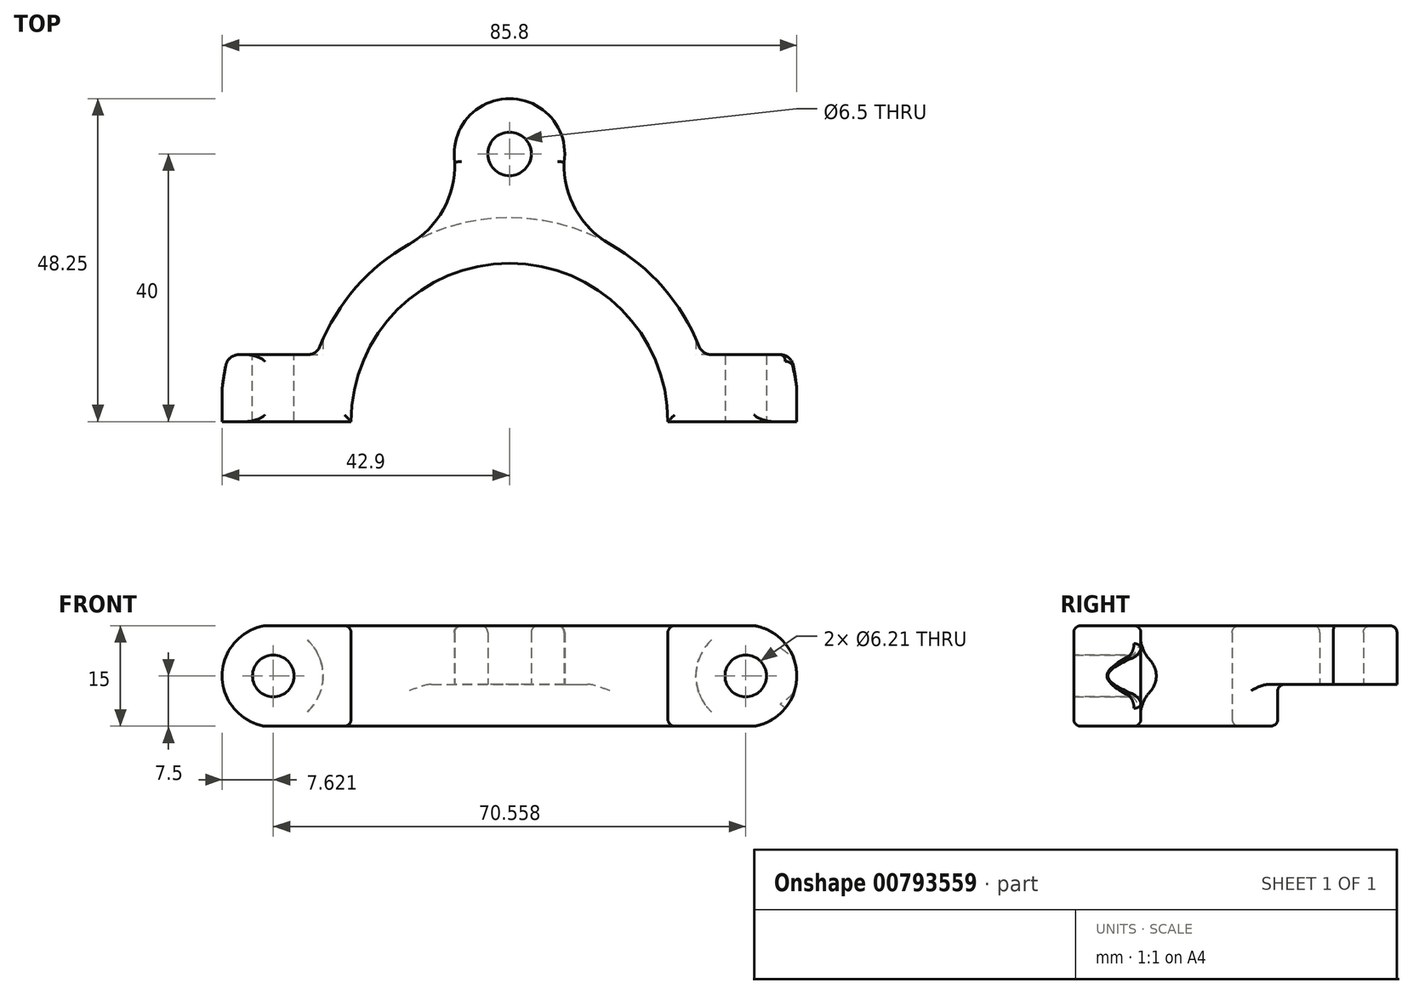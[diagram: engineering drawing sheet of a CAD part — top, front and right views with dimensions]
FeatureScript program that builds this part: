
annotation { "Feature Type Name" : "Feature", "Feature Type Description" : "" }
export const myFeature = defineFeature(function(context is Context, id is Id, definition is map)
    precondition{}
    {
        {
            var Q0;
            Q0=qCreatedBy(makeId("Top.planeOp"),FACE);
            var sketch = newSketch(context, id + "F0", { "sketchPlane" : qUnion([Q0])});
            skArc(sketch, "E0", {"start": v(23.65, 0) * mm, "mid": v(0, 23.65) * mm, "end": v(-23.65, 0) * mm});
            skLineSegment(sketch, "E1", {"start": v(-43.2, 0) * mm, "end": v(-23.65, 0) * mm});
            skLineSegment(sketch, "E2.0", {"start": v(-40.4, 10) * mm, "end": v(-30.15, 10) * mm});
            skArc(sketch, "E3", {"start": v(-42.37, 8.39) * mm, "mid": v(-42.99, 4.21) * mm, "end": v(-43.2, 0) * mm});
            skPoint(sketch, "E4.orphan", {"position": v(-60.74, 0) * mm});
            skArc(sketch, "E5.trimOffspring", {"start": v(43.2, 0) * mm, "mid": v(42.99, 4.21) * mm, "end": v(42.37, 8.39) * mm});
            skLineSegment(sketch, "E6.trimOffspring", {"start": v(30.15, 10) * mm, "end": v(40.4, 10) * mm});
            skLineSegment(sketch, "E7.trimOffspring", {"start": v(23.65, 0) * mm, "end": v(43.2, 0) * mm});
            skArc(sketch, "E8.trimOffspring", {"start": v(28.3, 11.26) * mm, "mid": v(27.77, 12.48) * mm, "end": v(27.2, 13.68) * mm});
            skLineSegment(sketch, "E9", {"start": v(0, 0) * mm, "end": v(-41.84, 41.84) * mm, "construction": true});
            skArc(sketch, "E10.trimOffspring", {"start": v(-27.2, 13.68) * mm, "mid": v(-27.77, 12.48) * mm, "end": v(-28.3, 11.26) * mm});
            skPoint(sketch, "E11.visualSharp", {"position": v(-15, 26.5) * mm});
            skPoint(sketch, "E12.visualSharp", {"position": v(-26.5, 15) * mm});
            skArc(sketch, "E13.trimOffspring", {"start": v(28.3, 11.26) * mm, "mid": v(22.45, 20.57) * mm, "end": v(13.68, 27.2) * mm});
            skPoint(sketch, "E14.visualSharp", {"position": v(-28.76, 10) * mm});
            skArc(sketch, "E14.filletArc", {"start": v(-30.15, 10) * mm, "mid": v(-29.03, 10.34) * mm, "end": v(-28.3, 11.26) * mm});
            skPoint(sketch, "E15.visualSharp", {"position": v(28.76, 10) * mm});
            skArc(sketch, "E15.filletArc", {"start": v(28.3, 11.26) * mm, "mid": v(29.03, 10.34) * mm, "end": v(30.15, 10) * mm});
            skPoint(sketch, "E16.visualSharp", {"position": v(42.02, 10) * mm});
            skArc(sketch, "E16.filletArc", {"start": v(42.37, 8.39) * mm, "mid": v(41.68, 9.55) * mm, "end": v(40.4, 10) * mm});
            skPoint(sketch, "E17.visualSharp", {"position": v(-42.02, 10) * mm});
            skArc(sketch, "E17.filletArc", {"start": v(-40.4, 10) * mm, "mid": v(-41.68, 9.55) * mm, "end": v(-42.37, 8.39) * mm});
            skCircle(sketch, "E18", {"center": v(0, 40) * mm, "radius": 3.25 * mm});
            skArc(sketch, "E19.0", {"start": v(8.16, 38.77) * mm, "mid": v(0, 48.25) * mm, "end": v(-8.16, 38.77) * mm});
            skPoint(sketch, "E12.filletArc.end.orphan", {"position": v(-27.53, 15.94) * mm});
            skPoint(sketch, "E11.filletArc.end.orphan", {"position": v(-13.68, 27.2) * mm});
            skPoint(sketch, "E11.filletArc.start.orphan", {"position": v(-15.94, 27.53) * mm});
            skPoint(sketch, "E20.MirrorCS.end.orphan", {"position": v(27.53, 15.94) * mm});
            skPoint(sketch, "E20.MirrorCS.start.orphan", {"position": v(15.94, 27.53) * mm});
            skPoint(sketch, "E21.MirrorCS.end.orphan", {"position": v(13.68, 27.2) * mm});
            skLineSegment(sketch, "E22", {"start": v(0, 40) * mm, "end": v(-18.23, 40) * mm});
            skArc(sketch, "E23", {"start": v(-15, 26.5) * mm, "mid": v(-9.6, 32.23) * mm, "end": v(-8.25, 40) * mm});
            skPoint(sketch, "E23.endSnap0", {"position": v(-9.12, 40) * mm});
            skArc(sketch, "E24.MirrorCS", {"start": v(15, 26.5) * mm, "mid": v(9.6, 32.23) * mm, "end": v(8.25, 40) * mm});
            skArc(sketch, "E25.trimOffspring", {"start": v(-13.68, 27.2) * mm, "mid": v(-22.45, 20.57) * mm, "end": v(-28.3, 11.26) * mm});
            skSolve(sketch);
        }
        {
            var Q0;
            Q0 = qSketchRegion(id + "F0", true);
            extrude(context, id + "F1", {"entities" : qUnion([Q0]), "depth" : 15 * mm, "offsetDistance" : 25 * mm});
        }
        {
            var Q0;
            Q0 = qSketchRegion(id + "F0", true);
            extrude(context, id + "F2", {"entities" : qUnion([Q0]), "operationType" : NewBodyOperationType.ADD, "depth" : 15 * mm, "offsetDistance" : 25 * mm});
        }
        {
            var Q0;
            Q0=makeQuery(id+"F1.opExtrude","SWEPT_FACE",FACE,{"disambiguationData":[OSD([sQuery(id+"F0.wireOp",EDGE,"E2.0")])]});
            var sketch = newSketch(context, id + "F3", { "sketchPlane" : qUnion([Q0])});
            skLineSegment(sketch, "E26", {"start": v(40.4, 0) * mm, "end": v(30.15, 15) * mm, "construction": true});
            skLineSegment(sketch, "E27", {"start": v(30.15, 15) * mm, "end": v(30.15, 0) * mm});
            skLineSegment(sketch, "E28", {"start": v(30.15, 0) * mm, "end": v(40.4, 15) * mm, "construction": true});
            skCircle(sketch, "E29", {"center": v(35.28, 7.5) * mm, "radius": 3.1 * mm});
            skCircle(sketch, "E30.MirrorC", {"center": v(-35.28, 7.5) * mm, "radius": 3.1 * mm});
            skSolve(sketch);
        }
        {
            var Q0;
            Q0=makeQuery(id+"F3.imprint","IMPRINT",FACE,{"disambiguationData":[TD([[makeQuery(id+"F3.imprint","IMPRINT",EDGE,{"derivedFrom":sQuery(id+"F3.wireOp",EDGE,"E29")}),1.0]])]});
            var Q1;
            Q1=makeQuery(id+"F3.imprint","IMPRINT",FACE,{"disambiguationData":[TD([[makeQuery(id+"F3.imprint","IMPRINT",EDGE,{"derivedFrom":sQuery(id+"F3.wireOp",EDGE,"E30.MirrorC")}),-1.0]])]});
            var Q2;
            Q2=sQuery(id+"F3.wireOp",EDGE,"E29");
            var Q3;
            Q3=sQuery(id+"F3.wireOp",EDGE,"E30.MirrorC");
            extrude(context, id + "F4", {"entities" : qUnion([Q0, Q1]), "operationType" : NewBodyOperationType.REMOVE, "surfaceEntities" : qUnion([Q2, Q3]), "endBound" : BoundingType.THROUGH_ALL, "oppositeDirection" : true, "depth" : 25 * mm, "offsetDistance" : 25 * mm});
        }
        {
            var Q0;
            Q0=makeQuery(id+"F1.opExtrude","SWEPT_FACE",FACE,{"disambiguationData":[OSD([sQuery(id+"F0.wireOp",EDGE,"E2.0")])]});
            var sketch = newSketch(context, id + "F5", { "sketchPlane" : qUnion([Q0])});
            skCircle(sketch, "E31", {"center": v(35.28, 7.5) * mm, "radius": 7.43 * mm});
            skCircle(sketch, "E32.MirrorC", {"center": v(-35.28, 7.5) * mm, "radius": 7.43 * mm});
            skSolve(sketch);
        }
        {
            var Q0;
            Q0 = qSketchRegion(id + "F5", true);
            extrude(context, id + "F6", {"entities" : qUnion([Q0]), "operationType" : NewBodyOperationType.REMOVE, "depth" : 25 * mm, "offsetDistance" : 25 * mm});
        }
        {
            var Q0;
            Q0=makeQuery(id+"F1.opExtrude","SWEPT_FACE",FACE,{"disambiguationData":[OSD([sQuery(id+"F0.wireOp",EDGE,"E7.trimOffspring")])]});
            var sketch = newSketch(context, id + "F7", { "sketchPlane" : qUnion([Q0])});
            skCircle(sketch, "E33.0", {"center": v(35.28, 7.5) * mm, "radius": 3.1 * mm});
            skArc(sketch, "E34", {"start": v(35.32, -0.12) * mm, "mid": v(42.9, 7.7) * mm, "end": v(34.94, 15.12) * mm});
            skLineSegment(sketch, "E35", {"start": v(34.94, 15.12) * mm, "end": v(56.6, 15.12) * mm});
            skLineSegment(sketch, "E36", {"start": v(56.6, 15.12) * mm, "end": v(56.6, 0) * mm});
            skLineSegment(sketch, "E37", {"start": v(56.6, 0) * mm, "end": v(35.32, -0.12) * mm});
            skLineSegment(sketch, "E38.MirrorCS", {"start": v(-34.94, 15.12) * mm, "end": v(-56.6, 15.12) * mm});
            skLineSegment(sketch, "E39.MirrorCS", {"start": v(-56.6, 15.12) * mm, "end": v(-56.6, 0) * mm});
            skLineSegment(sketch, "E40.MirrorCS", {"start": v(-56.6, 0) * mm, "end": v(-35.32, -0.12) * mm});
            skArc(sketch, "E41.MirrorCS", {"start": v(-35.32, -0.12) * mm, "mid": v(-42.9, 7.7) * mm, "end": v(-34.94, 15.12) * mm});
            skSolve(sketch);
        }
        {
            var Q0;
            Q0 = qSketchRegion(id + "F7", true);
            extrude(context, id + "F8", {"entities" : qUnion([Q0]), "operationType" : NewBodyOperationType.REMOVE, "endBound" : BoundingType.THROUGH_ALL, "oppositeDirection" : true, "depth" : 25 * mm, "offsetDistance" : 25 * mm});
        }
        {
            var Q0;
            Q0=makeQuery(id+"F1.opExtrude","CAP_FACE",FACE,{"disambiguationData":[OSD([sQuery(id+"F0.wireOp",EDGE,"E0"),sQuery(id+"F0.wireOp",EDGE,"E1"),sQuery(id+"F0.wireOp",EDGE,"E2.0"),sQuery(id+"F0.wireOp",EDGE,"E3"),sQuery(id+"F0.wireOp",EDGE,"E5.trimOffspring"),sQuery(id+"F0.wireOp",EDGE,"E6.trimOffspring"),sQuery(id+"F0.wireOp",EDGE,"E7.trimOffspring"),sQuery(id+"F0.wireOp",EDGE,"E13.trimOffspring"),sQuery(id+"F0.wireOp",EDGE,"E14.filletArc"),sQuery(id+"F0.wireOp",EDGE,"E15.filletArc"),sQuery(id+"F0.wireOp",EDGE,"E16.filletArc"),sQuery(id+"F0.wireOp",EDGE,"E17.filletArc"),sQuery(id+"F0.wireOp",EDGE,"E18"),sQuery(id+"F0.wireOp",EDGE,"E19.0"),sQuery(id+"F0.wireOp",EDGE,"E23"),sQuery(id+"F0.wireOp",EDGE,"E24.MirrorCS"),sQuery(id+"F0.wireOp",EDGE,"E25.trimOffspring")])],"isStart":true});
            var sketch = newSketch(context, id + "F9", { "sketchPlane" : qUnion([Q0])});
            skArc(sketch, "E42.0", {"start": v(23.65, 0) * mm, "mid": v(0, -23.65) * mm, "end": v(-23.65, 0) * mm});
            skArc(sketch, "E42.1", {"start": v(15, -26.5) * mm, "mid": v(-10.1, -28.72) * mm, "end": v(-28.3, -11.26) * mm});
            skArc(sketch, "E43.0", {"start": v(28.3, -11.26) * mm, "mid": v(22.95, -20.01) * mm, "end": v(15, -26.5) * mm});
            skPoint(sketch, "E44.orphan", {"position": v(-15, -26.5) * mm});
            skSolve(sketch);
        }
        {
            var Q0;
            Q0=makeQuery(id+"F9.imprint","IMPRINT",FACE,{"disambiguationData":[TD([[makeQuery(id+"F9.imprint","IMPRINT",EDGE,{"derivedFrom":makeQuery(id+"F1.opExtrude","CAP_EDGE",EDGE,{"disambiguationData":[OSD([sQuery(id+"F0.wireOp",EDGE,"E18")])],"isStart":true})}),1.0]])]});
            extrude(context, id + "F10", {"entities" : qUnion([Q0]), "operationType" : NewBodyOperationType.REMOVE, "oppositeDirection" : true, "depth" : 6.25 * mm, "offsetDistance" : 25 * mm});
        }
        {
            var Q0;
            Q0=makeQuery(id+"F10.boolean.opBoolean","COPY",EDGE,{"derivedFrom":makeQuery(id+"F10.opExtrude","CAP_EDGE",EDGE,{"disambiguationData":[OSD([sQuery(id+"F9.wireOp",EDGE,"E42.1")])],"isStart":false})});
            var Q1;
            Q1=makeQuery(id+"F10.boolean.opBoolean","COPY",EDGE,{"derivedFrom":makeQuery(id+"F10.opExtrude","CAP_EDGE",EDGE,{"disambiguationData":[OSD([sQuery(id+"F0.wireOp",EDGE,"E24.MirrorCS")])],"isStart":false})});
            var Q2;
            Q2=makeQuery(id+"F10.boolean.opBoolean","COPY",EDGE,{"derivedFrom":makeQuery(id+"F10.opExtrude","CAP_EDGE",EDGE,{"disambiguationData":[OSD([sQuery(id+"F0.wireOp",EDGE,"E19.0")])],"isStart":false})});
            var Q3;
            Q3=makeQuery(id+"F10.boolean.opBoolean","COPY",EDGE,{"derivedFrom":makeQuery(id+"F10.opExtrude","CAP_EDGE",EDGE,{"disambiguationData":[OSD([sQuery(id+"F0.wireOp",EDGE,"E23")])],"isStart":false})});
            var Q4;
            Q4=makeQuery(id+"F10.boolean.opBoolean","MERGE",EDGE,{"derivedFrom":[makeQuery(id+"F1.opExtrude","CAP_EDGE",EDGE,{"disambiguationData":[OSD([sQuery(id+"F0.wireOp",EDGE,"E13.trimOffspring")])],"isStart":true}),makeQuery(id+"F1.opExtrude","CAP_EDGE",EDGE,{"disambiguationData":[OSD([sQuery(id+"F0.wireOp",EDGE,"E25.trimOffspring")])],"isStart":true}),makeQuery(id+"F10.opExtrude","CAP_EDGE",EDGE,{"disambiguationData":[OSD([sQuery(id+"F9.wireOp",EDGE,"E42.1")])],"isStart":true})]});
            var Q5;
            Q5=makeQuery(id+"F1.opExtrude","CAP_EDGE",EDGE,{"disambiguationData":[OSD([sQuery(id+"F0.wireOp",EDGE,"E0")])],"isStart":true});
            var Q6;
            Q6=makeQuery(id+"F1.opExtrude","CAP_FACE",FACE,{"disambiguationData":[OSD([sQuery(id+"F0.wireOp",EDGE,"E0"),sQuery(id+"F0.wireOp",EDGE,"E1"),sQuery(id+"F0.wireOp",EDGE,"E2.0"),sQuery(id+"F0.wireOp",EDGE,"E3"),sQuery(id+"F0.wireOp",EDGE,"E5.trimOffspring"),sQuery(id+"F0.wireOp",EDGE,"E6.trimOffspring"),sQuery(id+"F0.wireOp",EDGE,"E7.trimOffspring"),sQuery(id+"F0.wireOp",EDGE,"E13.trimOffspring"),sQuery(id+"F0.wireOp",EDGE,"E14.filletArc"),sQuery(id+"F0.wireOp",EDGE,"E15.filletArc"),sQuery(id+"F0.wireOp",EDGE,"E16.filletArc"),sQuery(id+"F0.wireOp",EDGE,"E17.filletArc"),sQuery(id+"F0.wireOp",EDGE,"E18"),sQuery(id+"F0.wireOp",EDGE,"E19.0"),sQuery(id+"F0.wireOp",EDGE,"E23"),sQuery(id+"F0.wireOp",EDGE,"E24.MirrorCS"),sQuery(id+"F0.wireOp",EDGE,"E25.trimOffspring")])],"isStart":true});
            var Q7;
            {var subQ0=sQuery(id+"F7.wireOp",EDGE,"E34");var subQ1=sQuery(id+"F0.wireOp",EDGE,"E7.trimOffspring");var subQ3=makeQuery(id+"F7.imprint","INTERSECT",VERTEX,{"derivedFrom":[makeQuery(id+"F1.opExtrude","CAP_EDGE",EDGE,{"disambiguationData":[OSD([subQ1])],"isStart":true}),subQ0]});Q7=makeQuery(id+"F8.boolean.opBoolean","INTERSECT",EDGE,{"disambiguationData":[OD(0.0)],"derivedFrom":[makeQuery(id+"F6.boolean.opBoolean","MERGE",FACE,{"derivedFrom":[makeQuery(id+"F1.opExtrude","SWEPT_FACE",FACE,{"disambiguationData":[OSD([sQuery(id+"F0.wireOp",EDGE,"E6.trimOffspring")])]}),makeQuery(id+"F6.opExtrude","CAP_FACE",FACE,{"disambiguationData":[OSD([sQuery(id+"F5.wireOp",EDGE,"E32.MirrorC")])],"isStart":true})]}),makeQuery(id+"F8.opExtrude","SWEPT_FACE",FACE,{"disambiguationData":[OSD([subQ0]),TDD([makeQuery(id+"F7.imprint","IMPRINT",EDGE,{"disambiguationData":[TD([[makeQuery(id+"F7.imprint","INTERSECT",VERTEX,{"derivedFrom":[subQ0,sQuery(id+"F7.wireOp",EDGE,"E37")]}),-1.0]])],"derivedFrom":subQ0}),makeQuery(id+"F7.imprint","IMPRINT",EDGE,{"disambiguationData":[TD([[subQ3,-1.0]])],"derivedFrom":subQ0}),makeQuery(id+"F7.imprint","IMPRINT",EDGE,{"disambiguationData":[TD([[makeQuery(id+"F7.imprint","INTERSECT",VERTEX,{"disambiguationData":[OD(1.0)],"derivedFrom":[subQ0,sQuery(id+"F7.wireOp",EDGE,"E35")]}),1.0]])],"derivedFrom":subQ0})])]})]});}
            var Q8;
            {var subQ0=sQuery(id+"F7.wireOp",EDGE,"E34");var subQ1=sQuery(id+"F0.wireOp",EDGE,"E7.trimOffspring");var subQ3=makeQuery(id+"F7.imprint","INTERSECT",VERTEX,{"derivedFrom":[makeQuery(id+"F1.opExtrude","CAP_EDGE",EDGE,{"disambiguationData":[OSD([subQ1])],"isStart":true}),subQ0]});Q8=makeQuery(id+"F8.boolean.opBoolean","INTERSECT",EDGE,{"disambiguationData":[OD(0.0)],"derivedFrom":[makeQuery(id+"F1.opExtrude","SWEPT_FACE",FACE,{"disambiguationData":[OSD([sQuery(id+"F0.wireOp",EDGE,"E16.filletArc")])]}),makeQuery(id+"F8.opExtrude","SWEPT_FACE",FACE,{"disambiguationData":[OSD([subQ0]),TDD([makeQuery(id+"F7.imprint","IMPRINT",EDGE,{"disambiguationData":[TD([[makeQuery(id+"F7.imprint","INTERSECT",VERTEX,{"derivedFrom":[subQ0,sQuery(id+"F7.wireOp",EDGE,"E37")]}),-1.0]])],"derivedFrom":subQ0}),makeQuery(id+"F7.imprint","IMPRINT",EDGE,{"disambiguationData":[TD([[subQ3,-1.0]])],"derivedFrom":subQ0}),makeQuery(id+"F7.imprint","IMPRINT",EDGE,{"disambiguationData":[TD([[makeQuery(id+"F7.imprint","INTERSECT",VERTEX,{"disambiguationData":[OD(1.0)],"derivedFrom":[subQ0,sQuery(id+"F7.wireOp",EDGE,"E35")]}),1.0]])],"derivedFrom":subQ0})])]})]});}
            var Q9;
            {var subQ0=sQuery(id+"F7.wireOp",EDGE,"E34");var subQ1=sQuery(id+"F0.wireOp",EDGE,"E7.trimOffspring");var subQ3=makeQuery(id+"F7.imprint","INTERSECT",VERTEX,{"derivedFrom":[makeQuery(id+"F1.opExtrude","CAP_EDGE",EDGE,{"disambiguationData":[OSD([subQ1])],"isStart":true}),subQ0]});Q9=makeQuery(id+"F8.boolean.opBoolean","COPY",EDGE,{"derivedFrom":makeQuery(id+"F8.opExtrude","CAP_EDGE",EDGE,{"disambiguationData":[OSD([subQ0]),TDD([makeQuery(id+"F7.imprint","IMPRINT",EDGE,{"disambiguationData":[TD([[makeQuery(id+"F7.imprint","INTERSECT",VERTEX,{"derivedFrom":[subQ0,sQuery(id+"F7.wireOp",EDGE,"E37")]}),-1.0]])],"derivedFrom":subQ0}),makeQuery(id+"F7.imprint","IMPRINT",EDGE,{"disambiguationData":[TD([[subQ3,-1.0]])],"derivedFrom":subQ0}),makeQuery(id+"F7.imprint","IMPRINT",EDGE,{"disambiguationData":[TD([[makeQuery(id+"F7.imprint","INTERSECT",VERTEX,{"disambiguationData":[OD(1.0)],"derivedFrom":[subQ0,sQuery(id+"F7.wireOp",EDGE,"E35")]}),1.0]])],"derivedFrom":subQ0})])],"isStart":true})});}
            var Q10;
            {var subQ0=sQuery(id+"F7.wireOp",EDGE,"E41.MirrorCS");Q10=makeQuery(id+"F8.boolean.opBoolean","INTERSECT",EDGE,{"disambiguationData":[OD(0.0)],"derivedFrom":[makeQuery(id+"F6.boolean.opBoolean","MERGE",FACE,{"derivedFrom":[makeQuery(id+"F1.opExtrude","SWEPT_FACE",FACE,{"disambiguationData":[OSD([sQuery(id+"F0.wireOp",EDGE,"E2.0")])]}),makeQuery(id+"F6.opExtrude","CAP_FACE",FACE,{"disambiguationData":[OSD([sQuery(id+"F5.wireOp",EDGE,"E31")])],"isStart":true})]}),makeQuery(id+"F8.opExtrude","SWEPT_FACE",FACE,{"disambiguationData":[OSD([subQ0]),TDD([makeQuery(id+"F7.imprint","IMPRINT",EDGE,{"disambiguationData":[TD([[makeQuery(id+"F7.imprint","INTERSECT",VERTEX,{"derivedFrom":[sQuery(id+"F7.wireOp",EDGE,"E40.MirrorCS"),subQ0]}),-1.0]])],"derivedFrom":subQ0})])]})]});}
            var Q11;
            {var subQ0=sQuery(id+"F7.wireOp",EDGE,"E41.MirrorCS");Q11=makeQuery(id+"F8.boolean.opBoolean","COPY",EDGE,{"derivedFrom":makeQuery(id+"F8.opExtrude","CAP_EDGE",EDGE,{"disambiguationData":[OSD([subQ0]),TDD([makeQuery(id+"F7.imprint","IMPRINT",EDGE,{"disambiguationData":[TD([[makeQuery(id+"F7.imprint","INTERSECT",VERTEX,{"derivedFrom":[sQuery(id+"F7.wireOp",EDGE,"E40.MirrorCS"),subQ0]}),-1.0]])],"derivedFrom":subQ0})])],"isStart":true})});}
            var Q12;
            Q12=makeQuery(id+"F1.opExtrude","CAP_FACE",FACE,{"disambiguationData":[OSD([sQuery(id+"F0.wireOp",EDGE,"E0"),sQuery(id+"F0.wireOp",EDGE,"E1"),sQuery(id+"F0.wireOp",EDGE,"E2.0"),sQuery(id+"F0.wireOp",EDGE,"E3"),sQuery(id+"F0.wireOp",EDGE,"E5.trimOffspring"),sQuery(id+"F0.wireOp",EDGE,"E6.trimOffspring"),sQuery(id+"F0.wireOp",EDGE,"E7.trimOffspring"),sQuery(id+"F0.wireOp",EDGE,"E13.trimOffspring"),sQuery(id+"F0.wireOp",EDGE,"E14.filletArc"),sQuery(id+"F0.wireOp",EDGE,"E15.filletArc"),sQuery(id+"F0.wireOp",EDGE,"E16.filletArc"),sQuery(id+"F0.wireOp",EDGE,"E17.filletArc"),sQuery(id+"F0.wireOp",EDGE,"E18"),sQuery(id+"F0.wireOp",EDGE,"E19.0"),sQuery(id+"F0.wireOp",EDGE,"E23"),sQuery(id+"F0.wireOp",EDGE,"E24.MirrorCS"),sQuery(id+"F0.wireOp",EDGE,"E25.trimOffspring")])],"isStart":false});
            var Q13;
            {var subQ0=sQuery(id+"F7.wireOp",EDGE,"E41.MirrorCS");Q13=makeQuery(id+"F8.boolean.opBoolean","INTERSECT",EDGE,{"disambiguationData":[OD(1.0)],"derivedFrom":[makeQuery(id+"F6.boolean.opBoolean","MERGE",FACE,{"derivedFrom":[makeQuery(id+"F1.opExtrude","SWEPT_FACE",FACE,{"disambiguationData":[OSD([sQuery(id+"F0.wireOp",EDGE,"E2.0")])]}),makeQuery(id+"F6.opExtrude","CAP_FACE",FACE,{"disambiguationData":[OSD([sQuery(id+"F5.wireOp",EDGE,"E31")])],"isStart":true})]}),makeQuery(id+"F8.opExtrude","SWEPT_FACE",FACE,{"disambiguationData":[OSD([subQ0]),TDD([makeQuery(id+"F7.imprint","IMPRINT",EDGE,{"disambiguationData":[TD([[makeQuery(id+"F7.imprint","INTERSECT",VERTEX,{"derivedFrom":[sQuery(id+"F7.wireOp",EDGE,"E40.MirrorCS"),subQ0]}),-1.0]])],"derivedFrom":subQ0})])]})]});}
            var Q14;
            {var subQ0=sQuery(id+"F7.wireOp",EDGE,"E34");var subQ1=sQuery(id+"F0.wireOp",EDGE,"E7.trimOffspring");var subQ3=makeQuery(id+"F7.imprint","INTERSECT",VERTEX,{"derivedFrom":[makeQuery(id+"F1.opExtrude","CAP_EDGE",EDGE,{"disambiguationData":[OSD([subQ1])],"isStart":true}),subQ0]});Q14=makeQuery(id+"F8.boolean.opBoolean","INTERSECT",EDGE,{"disambiguationData":[OD(1.0)],"derivedFrom":[makeQuery(id+"F6.boolean.opBoolean","MERGE",FACE,{"derivedFrom":[makeQuery(id+"F1.opExtrude","SWEPT_FACE",FACE,{"disambiguationData":[OSD([sQuery(id+"F0.wireOp",EDGE,"E6.trimOffspring")])]}),makeQuery(id+"F6.opExtrude","CAP_FACE",FACE,{"disambiguationData":[OSD([sQuery(id+"F5.wireOp",EDGE,"E32.MirrorC")])],"isStart":true})]}),makeQuery(id+"F8.opExtrude","SWEPT_FACE",FACE,{"disambiguationData":[OSD([subQ0]),TDD([makeQuery(id+"F7.imprint","IMPRINT",EDGE,{"disambiguationData":[TD([[makeQuery(id+"F7.imprint","INTERSECT",VERTEX,{"derivedFrom":[subQ0,sQuery(id+"F7.wireOp",EDGE,"E37")]}),-1.0]])],"derivedFrom":subQ0}),makeQuery(id+"F7.imprint","IMPRINT",EDGE,{"disambiguationData":[TD([[subQ3,-1.0]])],"derivedFrom":subQ0}),makeQuery(id+"F7.imprint","IMPRINT",EDGE,{"disambiguationData":[TD([[makeQuery(id+"F7.imprint","INTERSECT",VERTEX,{"disambiguationData":[OD(1.0)],"derivedFrom":[subQ0,sQuery(id+"F7.wireOp",EDGE,"E35")]}),1.0]])],"derivedFrom":subQ0})])]})]});}
            var Q15;
            {var subQ0=sQuery(id+"F7.wireOp",EDGE,"E34");var subQ1=sQuery(id+"F0.wireOp",EDGE,"E7.trimOffspring");var subQ3=makeQuery(id+"F7.imprint","INTERSECT",VERTEX,{"derivedFrom":[makeQuery(id+"F1.opExtrude","CAP_EDGE",EDGE,{"disambiguationData":[OSD([subQ1])],"isStart":true}),subQ0]});Q15=makeQuery(id+"F8.boolean.opBoolean","INTERSECT",EDGE,{"disambiguationData":[OD(1.0)],"derivedFrom":[makeQuery(id+"F1.opExtrude","SWEPT_FACE",FACE,{"disambiguationData":[OSD([sQuery(id+"F0.wireOp",EDGE,"E16.filletArc")])]}),makeQuery(id+"F8.opExtrude","SWEPT_FACE",FACE,{"disambiguationData":[OSD([subQ0]),TDD([makeQuery(id+"F7.imprint","IMPRINT",EDGE,{"disambiguationData":[TD([[makeQuery(id+"F7.imprint","INTERSECT",VERTEX,{"derivedFrom":[subQ0,sQuery(id+"F7.wireOp",EDGE,"E37")]}),-1.0]])],"derivedFrom":subQ0}),makeQuery(id+"F7.imprint","IMPRINT",EDGE,{"disambiguationData":[TD([[subQ3,-1.0]])],"derivedFrom":subQ0}),makeQuery(id+"F7.imprint","IMPRINT",EDGE,{"disambiguationData":[TD([[makeQuery(id+"F7.imprint","INTERSECT",VERTEX,{"disambiguationData":[OD(1.0)],"derivedFrom":[subQ0,sQuery(id+"F7.wireOp",EDGE,"E35")]}),1.0]])],"derivedFrom":subQ0})])]})]});}
            var Q16;
            {var subQ0=sQuery(id+"F7.wireOp",EDGE,"E34");var subQ1=sQuery(id+"F0.wireOp",EDGE,"E7.trimOffspring");var subQ3=makeQuery(id+"F7.imprint","INTERSECT",VERTEX,{"derivedFrom":[makeQuery(id+"F1.opExtrude","CAP_EDGE",EDGE,{"disambiguationData":[OSD([subQ1])],"isStart":true}),subQ0]});Q16=makeQuery(id+"F8.boolean.opBoolean","INTERSECT",EDGE,{"derivedFrom":[makeQuery(id+"F1.opExtrude","SWEPT_FACE",FACE,{"disambiguationData":[OSD([sQuery(id+"F0.wireOp",EDGE,"E5.trimOffspring")])]}),makeQuery(id+"F8.opExtrude","SWEPT_FACE",FACE,{"disambiguationData":[OSD([subQ0]),TDD([makeQuery(id+"F7.imprint","IMPRINT",EDGE,{"disambiguationData":[TD([[makeQuery(id+"F7.imprint","INTERSECT",VERTEX,{"derivedFrom":[subQ0,sQuery(id+"F7.wireOp",EDGE,"E37")]}),-1.0]])],"derivedFrom":subQ0}),makeQuery(id+"F7.imprint","IMPRINT",EDGE,{"disambiguationData":[TD([[subQ3,-1.0]])],"derivedFrom":subQ0}),makeQuery(id+"F7.imprint","IMPRINT",EDGE,{"disambiguationData":[TD([[makeQuery(id+"F7.imprint","INTERSECT",VERTEX,{"disambiguationData":[OD(1.0)],"derivedFrom":[subQ0,sQuery(id+"F7.wireOp",EDGE,"E35")]}),1.0]])],"derivedFrom":subQ0})])]})]});}
            var Q17;
            {var subQ0=sQuery(id+"F7.wireOp",EDGE,"E41.MirrorCS");Q17=makeQuery(id+"F8.boolean.opBoolean","INTERSECT",EDGE,{"disambiguationData":[OD(1.0)],"derivedFrom":[makeQuery(id+"F1.opExtrude","SWEPT_FACE",FACE,{"disambiguationData":[OSD([sQuery(id+"F0.wireOp",EDGE,"E17.filletArc")])]}),makeQuery(id+"F8.opExtrude","SWEPT_FACE",FACE,{"disambiguationData":[OSD([subQ0]),TDD([makeQuery(id+"F7.imprint","IMPRINT",EDGE,{"disambiguationData":[TD([[makeQuery(id+"F7.imprint","INTERSECT",VERTEX,{"derivedFrom":[sQuery(id+"F7.wireOp",EDGE,"E40.MirrorCS"),subQ0]}),-1.0]])],"derivedFrom":subQ0})])]})]});}
            var Q18;
            {var subQ0=sQuery(id+"F7.wireOp",EDGE,"E41.MirrorCS");Q18=makeQuery(id+"F8.boolean.opBoolean","INTERSECT",EDGE,{"derivedFrom":[makeQuery(id+"F1.opExtrude","SWEPT_FACE",FACE,{"disambiguationData":[OSD([sQuery(id+"F0.wireOp",EDGE,"E3")])]}),makeQuery(id+"F8.opExtrude","SWEPT_FACE",FACE,{"disambiguationData":[OSD([subQ0]),TDD([makeQuery(id+"F7.imprint","IMPRINT",EDGE,{"disambiguationData":[TD([[makeQuery(id+"F7.imprint","INTERSECT",VERTEX,{"derivedFrom":[sQuery(id+"F7.wireOp",EDGE,"E40.MirrorCS"),subQ0]}),-1.0]])],"derivedFrom":subQ0})])]})]});}
            var Q19;
            {var subQ0=sQuery(id+"F7.wireOp",EDGE,"E41.MirrorCS");Q19=makeQuery(id+"F8.boolean.opBoolean","INTERSECT",EDGE,{"disambiguationData":[OD(0.0)],"derivedFrom":[makeQuery(id+"F1.opExtrude","SWEPT_FACE",FACE,{"disambiguationData":[OSD([sQuery(id+"F0.wireOp",EDGE,"E17.filletArc")])]}),makeQuery(id+"F8.opExtrude","SWEPT_FACE",FACE,{"disambiguationData":[OSD([subQ0]),TDD([makeQuery(id+"F7.imprint","IMPRINT",EDGE,{"disambiguationData":[TD([[makeQuery(id+"F7.imprint","INTERSECT",VERTEX,{"derivedFrom":[sQuery(id+"F7.wireOp",EDGE,"E40.MirrorCS"),subQ0]}),-1.0]])],"derivedFrom":subQ0})])]})]});}
            var Q20;
            Q20=makeQuery(id+"F1.opExtrude","CAP_EDGE",EDGE,{"disambiguationData":[OSD([sQuery(id+"F0.wireOp",EDGE,"E2.0")])],"isStart":true});
            fillet(context, id + "F11", {"entities" : qUnion([Q0, Q1, Q2, Q3, Q4, Q5, Q6, Q7, Q8, Q9, Q10, Q11, Q12, Q13, Q14, Q15, Q16, Q17, Q18, Q19, Q20]), "radius" : 1 * mm, "tangentPropagation" : true, "allowEdgeOverflow" : false});
        }
    });
